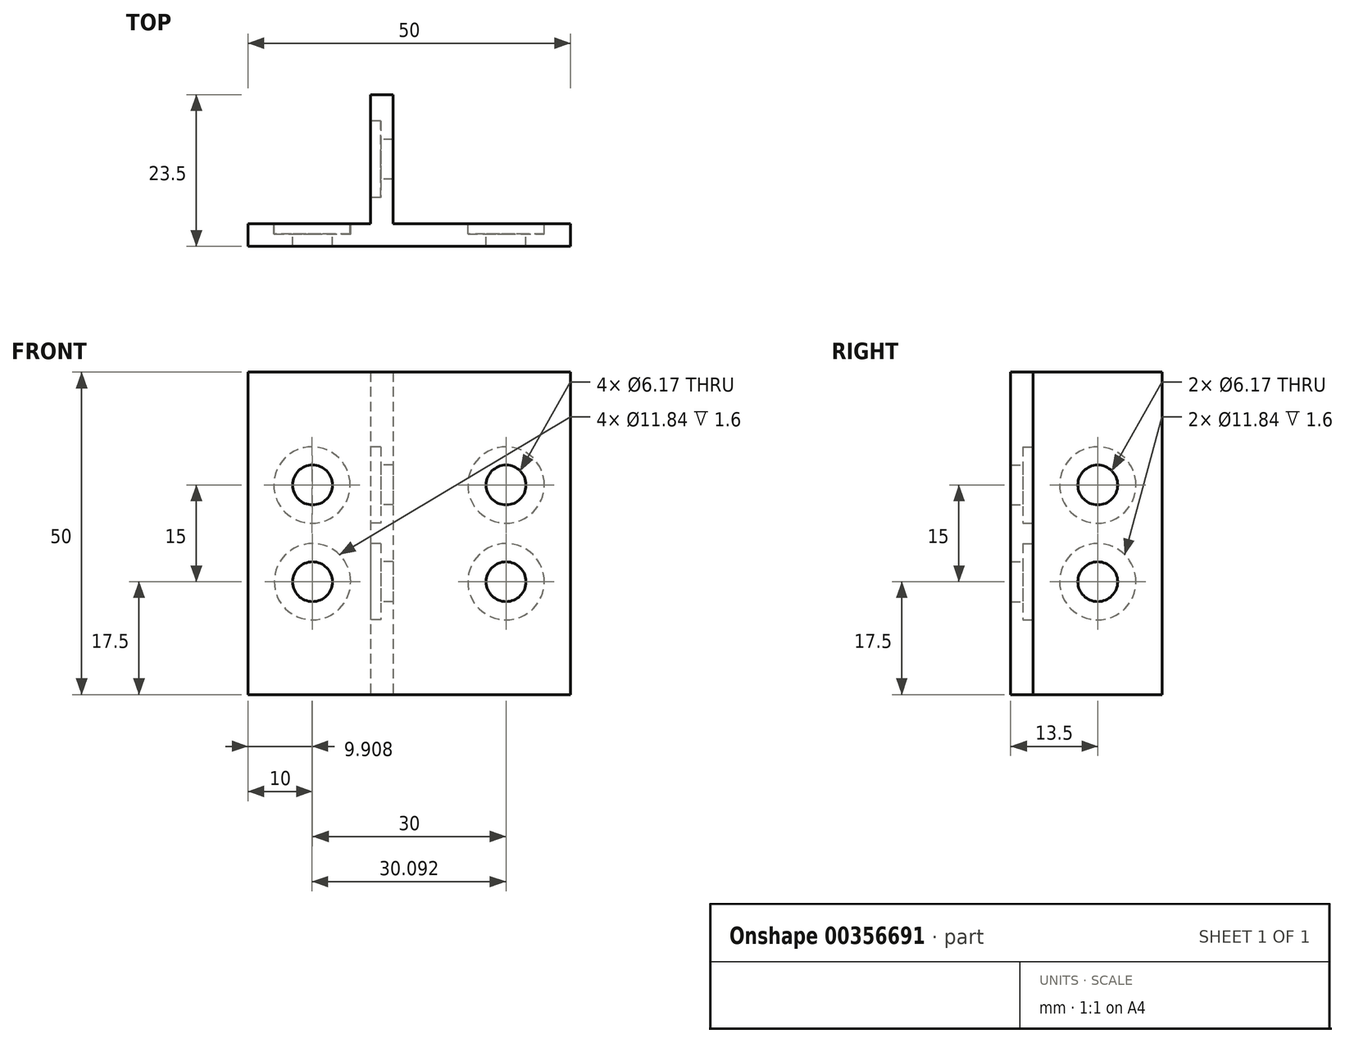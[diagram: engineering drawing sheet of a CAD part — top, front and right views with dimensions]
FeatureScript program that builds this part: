
annotation { "Feature Type Name" : "Feature", "Feature Type Description" : "" }
export const myFeature = defineFeature(function(context is Context, id is Id, definition is map)
    precondition{}
    {
        {
            var Q0;
            Q0=qCreatedBy(makeId("Front.planeOp"),FACE);
            var sketch = newSketch(context, id + "F0", { "sketchPlane" : qUnion([Q0])});
            skLineSegment(sketch, "E0.bottom", {"start": v(25, -25) * mm, "end": v(-25, -25) * mm});
            skLineSegment(sketch, "E0.top", {"start": v(25, 25) * mm, "end": v(-25, 25) * mm});
            skLineSegment(sketch, "E0.left", {"start": v(25, -25) * mm, "end": v(25, 25) * mm});
            skLineSegment(sketch, "E0.right", {"start": v(-25, -25) * mm, "end": v(-25, 25) * mm});
            skPoint(sketch, "E0.middle", {"position": v(0, 0) * mm});
            skSolve(sketch);
        }
        {
            var Q0;
            Q0=qSketchRegion(id+"F0",true);
            extrude(context, id + "F1", {"entities" : qUnion([Q0]), "depth" : 3.5 * mm});
        }
        {
            var Q0;
            Q0=qCreatedBy(makeId("Top.planeOp"),FACE);
            var sketch = newSketch(context, id + "F2", { "sketchPlane" : qUnion([Q0])});
            skLineSegment(sketch, "E1.bottom", {"start": v(-2.5, 0) * mm, "end": v(-6, 0) * mm});
            skLineSegment(sketch, "E1.top", {"start": v(-2.5, 20) * mm, "end": v(-6, 20) * mm});
            skLineSegment(sketch, "E1.left", {"start": v(-2.5, 0) * mm, "end": v(-2.5, 20) * mm});
            skLineSegment(sketch, "E1.right", {"start": v(-6, 0) * mm, "end": v(-6, 20) * mm});
            skSolve(sketch);
        }
        {
            var Q0;
            Q0=qSketchRegion(id+"F2",true);
            extrude(context, id + "F3", {"entities" : qUnion([Q0]), "operationType" : NewBodyOperationType.ADD, "endBound" : BoundingType.SYMMETRIC, "depth" : 50 * mm});
        }
        {
            var Q0;
            Q0=makeQuery(id+"F3.opExtrude","SWEPT_FACE",FACE,{"disambiguationData":[OSD([sQuery(id+"F2.wireOp",EDGE,"E1.right")])]});
            var sketch = newSketch(context, id + "F4", { "sketchPlane" : qUnion([Q0])});
            skCircle(sketch, "E2", {"center": v(-10, 7.5) * mm, "radius": 3.09 * mm});
            skCircle(sketch, "E3", {"center": v(-10, -7.5) * mm, "radius": 3.09 * mm});
            skLineSegment(sketch, "E4", {"start": v(-10, 7.5) * mm, "end": v(-10, 0) * mm});
            skLineSegment(sketch, "E5", {"start": v(-10, 0) * mm, "end": v(-10, -7.5) * mm});
            skLineSegment(sketch, "E6", {"start": v(-10, -7.5) * mm, "end": v(0, -7.5) * mm});
            skLineSegment(sketch, "E7", {"start": v(-10, 7.5) * mm, "end": v(0, 7.5) * mm});
            skSolve(sketch);
        }
        {
            var Q0;
            Q0=qSketchRegion(id+"F4",true);
            extrude(context, id + "F5", {"entities" : qUnion([Q0]), "operationType" : NewBodyOperationType.REMOVE, "oppositeDirection" : true, "depth" : 25 * mm});
        }
        {
            var Q0;
            Q0=makeQuery(id+"F3.opExtrude","SWEPT_FACE",FACE,{"disambiguationData":[OSD([sQuery(id+"F2.wireOp",EDGE,"E1.right")])]});
            var sketch = newSketch(context, id + "F6", { "sketchPlane" : qUnion([Q0])});
            skCircle(sketch, "E8", {"center": v(-10, 7.5) * mm, "radius": 5.92 * mm});
            skCircle(sketch, "E9", {"center": v(-10, -7.5) * mm, "radius": 5.92 * mm});
            skSolve(sketch);
        }
        {
            var Q0;
            Q0=qSketchRegion(id+"F6",true);
            extrude(context, id + "F7", {"entities" : qUnion([Q0]), "operationType" : NewBodyOperationType.REMOVE, "oppositeDirection" : true, "depth" : 1.6 * mm});
        }
        {
            var Q0;
            {var subQ4=sQuery(id+"F0.wireOp",EDGE,"E0.left");var subQ5=sQuery(id+"F0.wireOp",EDGE,"E0.top");var subQ6=sQuery(id+"F0.wireOp",EDGE,"E0.bottom");Q0=makeQuery(id+"F3.boolean.opBoolean","SPLIT",FACE,{"disambiguationData":[TD([makeQuery(id+"F1.opExtrude","SWEPT_FACE",FACE,{"disambiguationData":[OSD([subQ4])]})])],"derivedFrom":makeQuery(id+"F1.opExtrude","CAP_FACE",FACE,{"disambiguationData":[OSD([subQ6,subQ5,subQ4,sQuery(id+"F0.wireOp",EDGE,"E0.right")])],"isStart":true})});}
            var sketch = newSketch(context, id + "F8", { "sketchPlane" : qUnion([Q0])});
            skCircle(sketch, "E10", {"center": v(-15, 7.5) * mm, "radius": 3.09 * mm});
            skCircle(sketch, "E11", {"center": v(-15, -7.5) * mm, "radius": 3.09 * mm});
            skCircle(sketch, "E12", {"center": v(15, 7.5) * mm, "radius": 3.09 * mm});
            skCircle(sketch, "E13", {"center": v(15, -7.5) * mm, "radius": 3.09 * mm});
            skLineSegment(sketch, "E14", {"start": v(-15, 7.5) * mm, "end": v(-15, 0) * mm, "construction": true});
            skPoint(sketch, "E14.endSnap0", {"position": v(-25, 0) * mm});
            skLineSegment(sketch, "E15", {"start": v(-15, 0) * mm, "end": v(-15, -7.5) * mm, "construction": true});
            skLineSegment(sketch, "E16", {"start": v(-15, -7.5) * mm, "end": v(0, -7.5) * mm, "construction": true});
            skLineSegment(sketch, "E17", {"start": v(0, -7.5) * mm, "end": v(15, -7.5) * mm, "construction": true});
            skLineSegment(sketch, "E18", {"start": v(15, -7.5) * mm, "end": v(15, 0) * mm, "construction": true});
            skLineSegment(sketch, "E19", {"start": v(15, 0) * mm, "end": v(15, 7.5) * mm, "construction": true});
            skLineSegment(sketch, "E20", {"start": v(-15, 7.5) * mm, "end": v(0, 7.5) * mm, "construction": true});
            skLineSegment(sketch, "E21", {"start": v(0, 7.5) * mm, "end": v(15, 7.5) * mm, "construction": true});
            skSolve(sketch);
        }
        {
            var Q0;
            Q0=qSketchRegion(id+"F8",true);
            extrude(context, id + "F9", {"entities" : qUnion([Q0]), "operationType" : NewBodyOperationType.REMOVE, "oppositeDirection" : true, "depth" : 25 * mm});
        }
        {
            var Q0;
            {var subQ4=sQuery(id+"F0.wireOp",EDGE,"E0.left");var subQ5=sQuery(id+"F0.wireOp",EDGE,"E0.top");var subQ6=sQuery(id+"F0.wireOp",EDGE,"E0.bottom");Q0=makeQuery(id+"F3.boolean.opBoolean","SPLIT",FACE,{"disambiguationData":[TD([makeQuery(id+"F1.opExtrude","SWEPT_FACE",FACE,{"disambiguationData":[OSD([subQ4])]})])],"derivedFrom":makeQuery(id+"F1.opExtrude","CAP_FACE",FACE,{"disambiguationData":[OSD([subQ6,subQ5,subQ4,sQuery(id+"F0.wireOp",EDGE,"E0.right")])],"isStart":true})});}
            var sketch = newSketch(context, id + "F10", { "sketchPlane" : qUnion([Q0])});
            skCircle(sketch, "E22", {"center": v(-15, 7.5) * mm, "radius": 5.92 * mm});
            skCircle(sketch, "E23", {"center": v(-15, -7.5) * mm, "radius": 5.92 * mm});
            skCircle(sketch, "E24", {"center": v(15.1, 7.5) * mm, "radius": 5.92 * mm});
            skCircle(sketch, "E25", {"center": v(15, -7.5) * mm, "radius": 5.92 * mm});
            skSolve(sketch);
        }
        {
            var Q0;
            Q0=qSketchRegion(id+"F10",true);
            extrude(context, id + "F11", {"entities" : qUnion([Q0]), "operationType" : NewBodyOperationType.REMOVE, "oppositeDirection" : true, "depth" : 1.6 * mm});
        }
    });
